# Revit family: Grohe_ShowerMixer_194512433
name_source: partatom
category: Plumbing Fixtures
units: mm (PartAtom-declared; Revit-internal decimal feet)

## family parameters
Cut with Voids When Loaded = No
Host = Face
OmniClass Number = 23.45.05.00
OmniClass Title = Sanitary Equipment
Part Type = Normal
Room Calculation Point = No
Round Connector Dimension = Use Diameter
Shared = No

## types (1)
- Shower Mixer (194512433)
    Assembly Code = D2013
    AssetType = Fixed
    BIMObjectName = Grohe_ShowerMixer_194512433
    CO2NeutralProduction = GROHE is one of the first leading manufacturer within the sanitary industry having a CO2-neutral production.
    ClassificationName = Uniclass2015
    ClassificationValue = Pr_40_20_87_55
    Color = Grohe_Chrome
    Cost = 0 $
    Default Elevation = 0 mm  [stored 0 ft]
    Description = Shower Mixer
    DimensionsDocumentLink = https://cdn.cloud.grohe.com
    DocumentationCertificates = https://www.bimstore.co
    DocumentationInstallationGuide = https://www.bimstore.co
    DocumentationLiterature = https://www.bimstore.co
    DocumentationMaintenance = https://www.bimstore.co
    DocumentationTechnical = https://www.bimstore.co
    DurationUnit = Years
    EF000003 = 0
    EF000007 = true
    EF000008 = true
    EF000010 = true
    EF000040 = true
    EF000051 = 0
    EF000113 = true
    EF000125 = 0
    EF000301 = true
    EF000303 = true
    EF000329 = true
    EF000332 = true
    EF000443 = 0
    EF000634 = true
    EF000664 = true
    EF001187 = true
    EF001438 = true
    EF001469 = 0
    EF001656 = 0
    EF001707 = true
    EF002147 = 0
    EF002149 = true
    EF002169 = 0
    EF002286 = 0
    EF002594 = true
    EF002671 = true
    EF002677 = 0
    EF003454 = true
    EF003829 = true
    EF005084 = true
    EF005474 = true
    EF005545 = true
    EF005870 = true
    EF006485 = true
    EF006569 = true
    EF006974 = true
    EF008277 = true
    EF010904 = true
    EF011622 = true
    EF011623 = 0
    EF011625 = true
    EF011626 = true
    EF011628 = 0
    EF011779 = true
    EF012491 = true
    EF012637 = true
    EF012753 = 0
    EF013621 = true
    EF013633 = 0
    EF013956 = 0
    EF014578 = true
    EF015359 = true
    EF015760 = 0
    EF016731 = true
    EF020075 = Yes
    EF020103 = 0
    EF020348 = true
    EF020774 = 0
    EF020779 = true
    EF020780 = true
    EF020782 = 0
    EF020783 = 0
    EF020784 = true
    EF020785 = true
    EF020786 = 0
    EF020787 = true
    EF020789 = true
    EF020790 = true
    EF020792 = true
    EF020794 = true
    EF020797 = true
    EF020798 = true
    EF020799 = true
    EF020800 = 0
    EF020801 = true
    EF020803 = true
    EF020804 = 0
    EF020825 = true
    EF020826 = true
    EF020873 = true
    EF020966 = 0
    EF020967 = 0
    EF020969 = 0
    EF020970 = 0
    EF020971 = 0
    EF020989 = 0
    EF020990 = true
    EF021035 = true
    EF021038 = true
    EF021039 = true
    EF021040 = true
    EF021041 = 0
    EF021457 = 0
    EF021607 = true
    EF021652 = true
    EF021758 = true
    EF021760 = true
    EF021835 = true
    EF021855 = 0
    EF022116 = true
    EF022168 = true
    EF022182 = true
    EF022221 = 0
    EF022222 = true
    EF022223 = true
    EF022225 = true
    EF022252 = true
    EF022266 = 0
    EF022267 = true
    EF022268 = true
    EF022269 = true
    EF022337 = 0
    EF022338 = true
    EF022377 = true
    EF022393 = true
    EF022394 = true
    EF022397 = 0
    EF022398 = true
    EF022454 = 0
    EF022750 = true
    EF023140 = 0
    EF023452 = true
    EF023661 = 0
    EF023686 = true
    EF023687 = 0
    EF023688 = true
    EF023790 = true
    EF023957 = true
    EF024007 = 0
    EF024008 = 0
    EF024009 = 0
    EF024048 = 0
    EF024050 = 0
    EF024051 = true
    EF024076 = 0
    EF024078 = true
    EF024225 = true
    EF024471 = true
    EF024474 = true
    EF024492 = true
    EF024494 = true
    EF024495 = true
    EF024537 = 0
    EF024552 = true
    EF024553 = 0
    EF024554 = 0
    EF024736 = true
    EF024792 = 0
    EF024897 = true
    EF024921 = 0
    EF024922 = true
    EF025080 = true
    EF025091 = 0
    EF025093 = true
    EF025101 = true
    EF025104 = true
    EF025107 = true
    EF025221 = 0
    EF025247 = true
    EF025336 = true
    EFNL0001 = true
    Ecojoy = No
    ExpectedLife = 0
    Finish = Chrome
    FullRecyclabilityOfPlastic = All plastic components are fully recycable
    GROHESocialCommittment = green.grohe.com/social_engagement
    GROHESustainability = green.grohe.com
    IfcExportAs = IfcPipeFitting
    IfcExportType = IfcPipeFittingType
    Keynote = N16
    Manufacturer = Grohe
    ManufacturerName = Grohe
    Model = Shower Mixer
    ModelNumber = 194512433
    ModelReference = Shower Mixer
    NBSDescription = Shower fittings package
    NBSObjectName = Grohe - Shower fittings package
    NBSReference = 45-35-70/293
    NominalDepth = 0 mm  [stored 0 ft]
    NominalHeight = 0 mm  [stored 0 ft]
    NominalLength = 0 mm  [stored 0 ft]
    PrimaryMaterial = Grohe_Chrome
    ProductDescription = set for final installation for

33 961 000, 33 962 000, 33 963 000, 33 964 000, 33 965 000, 33 966 000, 35 501 000

without concealed body

metal lever

GROHE Long-Life finish

GROHE FastFixation escutcheon with covered fixation

escutcheon and shaft sealing

metal wall escutcheon

professional exclusive
    ProductNumber = 194512433
    ProductShortText = Single-lever shower mixer
    ProductType = Single Lever Mixer
    ProductionYear = 2023
    SustainabilityAward = green.grohe.com/awards
    SustainabilityReport = green.grohe.com/reporting
    TPIDocumentLink = https://cdn.cloud.grohe.com
    Type Comments = Shower Mixer
    TypeName = Shower Mixer
    URL = https://www.grohe.co.uk
    WarrantyDurationLabor = 0
    WarrantyDurationParts = 0
    WarrantyDurationUnit = Years
    _BSBibleVersion = 17
    _BimSpecGuid = 0
    _CurrentRevision = 1
    _DistributedBy = https://www.bimstore.co
    _ObjectUserGuide = https://www.bimstore.co

note: [stored X ft] marks values corroborated as IEEE doubles in the binary element streams (Revit-internal decimal feet)

## geometry (parser evidence)
native form markers: Sweep x2
no freeform markers — native parametric forms only
